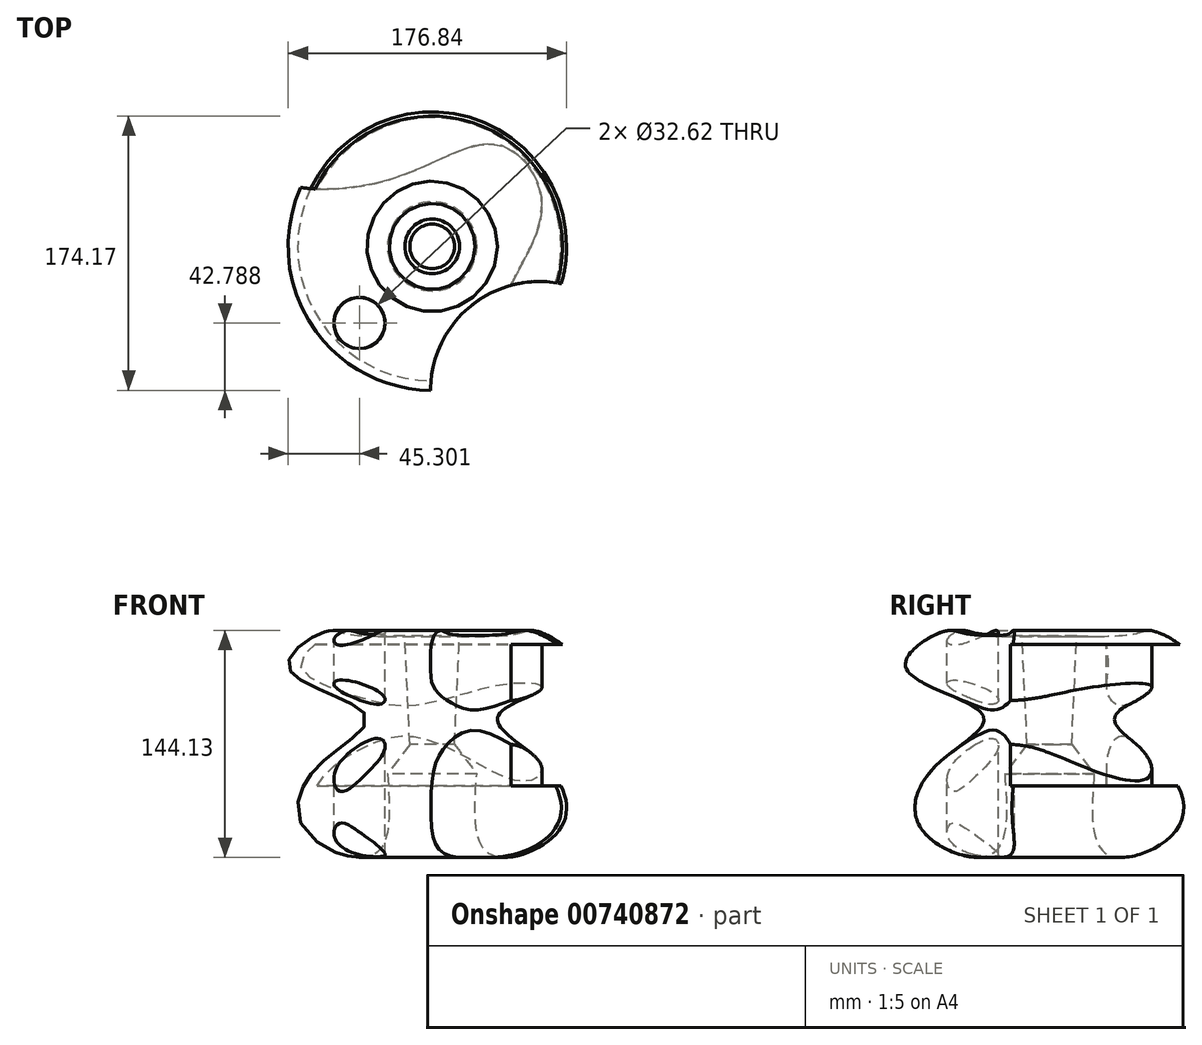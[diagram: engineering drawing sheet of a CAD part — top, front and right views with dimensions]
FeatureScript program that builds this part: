
annotation { "Feature Type Name" : "Feature", "Feature Type Description" : "" }
export const myFeature = defineFeature(function(context is Context, id is Id, definition is map)
    precondition{}
    {
        {
            var Q0;
            Q0=qCreatedBy(makeId("Front.planeOp"),FACE);
            var sketch = newSketch(context, id + "F0", { "sketchPlane" : qUnion([Q0])});
            skFitSpline(sketch, "E0", {"points": [v(0, 50.84) * mm, v(54.26, 51.82) * mm, v(66.97, 53.28) * mm, v(91.14, 30.3) * mm, v(42.04, 0) * mm, v(72.35, -32.26) * mm, v(81.14, -72.35) * mm, v(37.15, -88.48) * mm, v(28.35, -37.15) * mm], "startDerivative": vector(461.5, -14.43) * mm, "endDerivative": vector(34.4, 483.48) * mm});
            skLineSegment(sketch, "E1", {"start": v(28.35, -37.15) * mm, "end": v(14.18, -18.58) * mm});
            skLineSegment(sketch, "E2", {"start": v(0, 50.84) * mm, "end": v(0, 0) * mm, "construction": true});
            skLineSegment(sketch, "E3", {"start": v(17.37, 50.34) * mm, "end": v(14.18, -18.58) * mm});
            skSolve(sketch);
        }
        {
            var Q0;
            Q0=makeQuery(id+"F0.imprint","IMPRINT",FACE,{"disambiguationData":[TD([[makeQuery(id+"F0.imprint","IMPRINT",EDGE,{"derivedFrom":sQuery(id+"F0.wireOp",EDGE,"E0")}),-1.0]])]});
            var Q1;
            Q1=sQuery(id+"F0.wireOp",EDGE,"E2");
            revolve(context, id + "F1", {"surfaceOperationType" : NewSurfaceOperationType.NEW, "entities" : qUnion([Q0]), "axis" : qUnion([Q1]), "revolveType" : RevolveType.FULL});
        }
        {
            var Q0;
            Q0=qCreatedBy(makeId("Top.planeOp"),FACE);
            var sketch = newSketch(context, id + "F2", { "sketchPlane" : qUnion([Q0])});
            skFitSpline(sketch, "E4", {"points": [v(-103.67, 46.7) * mm, v(-26.2, 42.72) * mm, v(42.72, 64.37) * mm, v(69.5, 21.08) * mm, v(45, -47.28) * mm, v(82.6, -69.5) * mm, v(116.2, 0) * mm, v(66.07, 115.63) * mm, v(-33.6, 144.68) * mm, v(-90.57, 92.85) * mm, v(-103.67, 46.7) * mm]});
            skSolve(sketch);
        }
        {
            var Q0;
            Q0=makeQuery(id+"F2.imprint","IMPRINT",FACE,{"disambiguationData":[TD([[makeQuery(id+"F2.imprint","IMPRINT",EDGE,{"derivedFrom":sQuery(id+"F2.wireOp",EDGE,"E4")}),1.0]])]});
            extrude(context, id + "F3", {"entities" : qUnion([Q0]), "operationType" : NewBodyOperationType.REMOVE, "oppositeDirection" : true, "depth" : 89.84 * mm, "offsetDistance" : 25.4 * mm, "symmetric" : true});
        }
        {
            var Q0;
            Q0=qCreatedBy(makeId("Top.planeOp"),FACE);
            var sketch = newSketch(context, id + "F4", { "sketchPlane" : qUnion([Q0])});
            skCircle(sketch, "E5", {"center": v(-46.15, -48.65) * mm, "radius": 16.3 * mm});
            skCircle(sketch, "E6", {"center": v(68.17, -91.49) * mm, "radius": 69.18 * mm});
            skSolve(sketch);
        }
        {
            var Q0;
            Q0=makeQuery(id+"F4.imprint","IMPRINT",FACE,{"disambiguationData":[TD([[makeQuery(id+"F4.imprint","IMPRINT",EDGE,{"derivedFrom":sQuery(id+"F4.wireOp",EDGE,"E6")}),1.0]])]});
            var Q1;
            Q1 = qSketchRegion(id + "F4", true);
            var Q2;
            Q2=makeQuery(id+"F4.imprint","IMPRINT",FACE,{"disambiguationData":[TD([[makeQuery(id+"F4.imprint","IMPRINT",EDGE,{"derivedFrom":sQuery(id+"F4.wireOp",EDGE,"E5")}),1.0]])]});
            extrude(context, id + "F5", {"entities" : qUnion([Q0, Q1, Q2]), "operationType" : NewBodyOperationType.REMOVE, "oppositeDirection" : true, "depth" : 279.05 * mm, "offsetDistance" : 25.4 * mm, "symmetric" : true});
        }
    });
